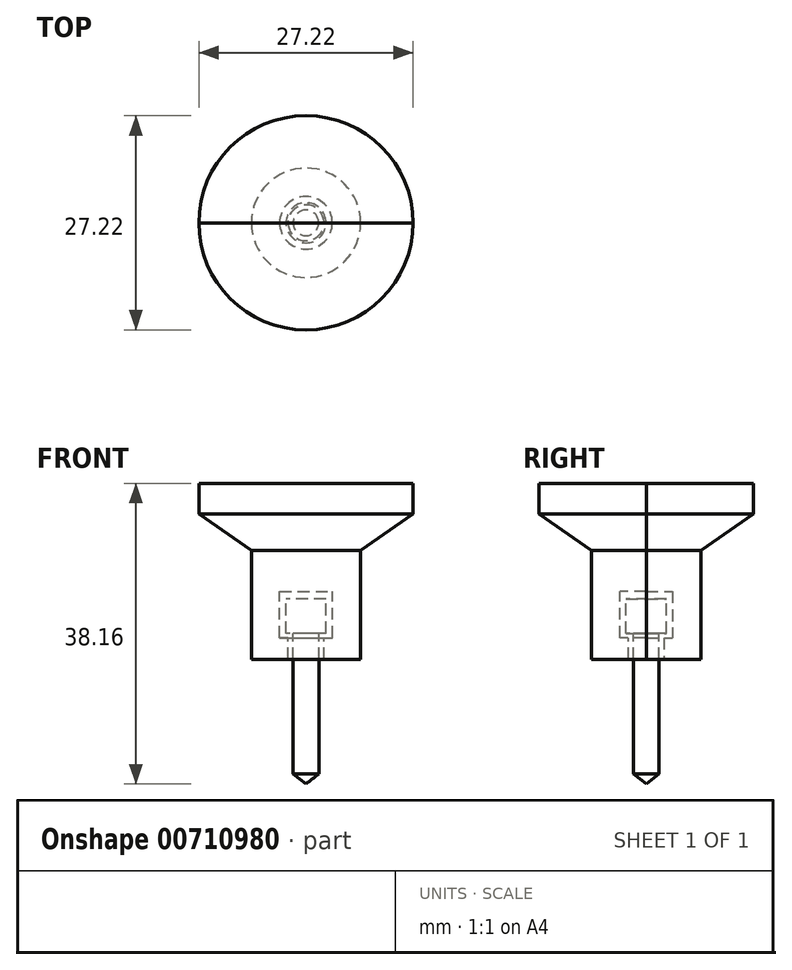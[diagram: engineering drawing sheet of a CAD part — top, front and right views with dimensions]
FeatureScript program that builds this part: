
annotation { "Feature Type Name" : "Feature", "Feature Type Description" : "" }
export const myFeature = defineFeature(function(context is Context, id is Id, definition is map)
    precondition{}
    {
        {
            var Q0;
            Q0=qCreatedBy(makeId("Front.planeOp"),FACE);
            var sketch = newSketch(context, id + "F0", { "sketchPlane" : qUnion([Q0])});
            skLineSegment(sketch, "E0", {"start": v(0, -11.65) * mm, "end": v(0, 11.84) * mm});
            skLineSegment(sketch, "E1", {"start": v(0, 11.84) * mm, "end": v(2.55, 11.84) * mm});
            skLineSegment(sketch, "E2", {"start": v(2.55, 11.84) * mm, "end": v(2.55, 7.47) * mm});
            skLineSegment(sketch, "E3", {"start": v(2.55, 7.47) * mm, "end": v(1.62, 7.47) * mm});
            skLineSegment(sketch, "E4", {"start": v(1.62, 7.47) * mm, "end": v(1.62, -10.39) * mm});
            skLineSegment(sketch, "E5", {"start": v(1.62, -10.39) * mm, "end": v(0, -11.65) * mm});
            skLineSegment(sketch, "E6", {"start": v(0, 26.51) * mm, "end": v(13.6, 26.51) * mm});
            skLineSegment(sketch, "E7", {"start": v(13.6, 26.51) * mm, "end": v(13.6, 22.6) * mm});
            skLineSegment(sketch, "E8", {"start": v(13.6, 22.6) * mm, "end": v(6.95, 18.02) * mm});
            skLineSegment(sketch, "E9", {"start": v(6.95, 18.02) * mm, "end": v(6.95, 4.16) * mm});
            skLineSegment(sketch, "E10", {"start": v(6.95, 4.16) * mm, "end": v(2.28, 4.16) * mm});
            skLineSegment(sketch, "E11", {"start": v(2.28, 4.16) * mm, "end": v(2.28, 6.92) * mm});
            skLineSegment(sketch, "E12", {"start": v(2.28, 6.92) * mm, "end": v(3.35, 6.92) * mm});
            skLineSegment(sketch, "E13", {"start": v(3.35, 6.92) * mm, "end": v(3.35, 12.81) * mm});
            skLineSegment(sketch, "E14", {"start": v(3.35, 12.81) * mm, "end": v(0, 12.81) * mm});
            skLineSegment(sketch, "E15", {"start": v(0, 12.81) * mm, "end": v(0, 26.51) * mm});
            skLineSegment(sketch, "E16", {"start": v(0, 32.7) * mm, "end": v(0, -23.84) * mm, "construction": true});
            skPoint(sketch, "E16.endSnap0", {"position": v(0, 19.66) * mm});
            skSolve(sketch);
        }
        {
            var Q0;
            Q0=makeQuery(id+"F0.imprint","IMPRINT",FACE,{"disambiguationData":[TD([[makeQuery(id+"F0.imprint","IMPRINT",EDGE,{"derivedFrom":sQuery(id+"F0.wireOp",EDGE,"E0")}),-1.0]])]});
            var Q1;
            Q1=sQuery(id+"F0.wireOp",EDGE,"E16");
            revolve(context, id + "F1", {"surfaceOperationType" : NewSurfaceOperationType.NEW, "entities" : qUnion([Q0]), "axis" : qUnion([Q1]), "revolveType" : RevolveType.FULL});
        }
        {
            var Q0;
            Q0=makeQuery(id+"F0.imprint","IMPRINT",FACE,{"disambiguationData":[TD([[makeQuery(id+"F0.imprint","IMPRINT",EDGE,{"derivedFrom":sQuery(id+"F0.wireOp",EDGE,"E6")}),-1.0]])]});
            var Q1;
            Q1=sQuery(id+"F0.wireOp",EDGE,"E16");
            revolve(context, id + "F2", {"surfaceOperationType" : NewSurfaceOperationType.NEW, "entities" : qUnion([Q0]), "axis" : qUnion([Q1]), "revolveType" : RevolveType.ONE_DIRECTION, "angle" : 180 * degree});
        }
        {
            var Q0;
            Q0=makeQuery(id+"F0.imprint","IMPRINT",FACE,{"disambiguationData":[TD([[makeQuery(id+"F0.imprint","IMPRINT",EDGE,{"derivedFrom":sQuery(id+"F0.wireOp",EDGE,"E6")}),-1.0]])]});
            var Q1;
            Q1=sQuery(id+"F0.wireOp",EDGE,"E16");
            revolve(context, id + "F3", {"surfaceOperationType" : NewSurfaceOperationType.NEW, "entities" : qUnion([Q0]), "axis" : qUnion([Q1]), "revolveType" : RevolveType.ONE_DIRECTION, "oppositeDirection" : true, "angle" : 180 * degree});
        }
    });
